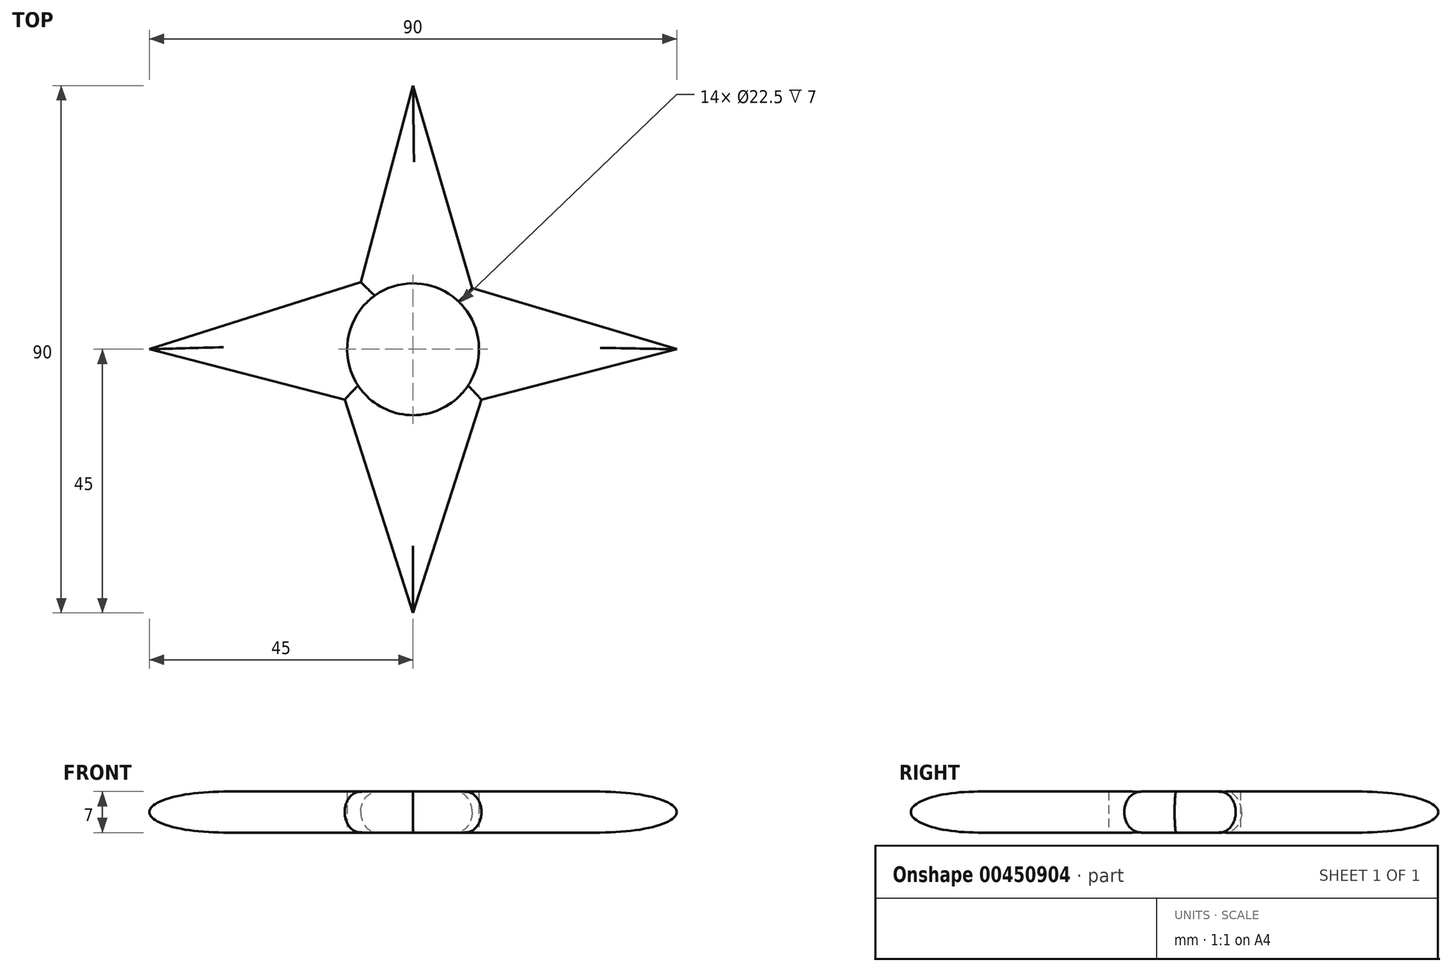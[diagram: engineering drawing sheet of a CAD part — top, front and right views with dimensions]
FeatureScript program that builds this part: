
annotation { "Feature Type Name" : "Feature", "Feature Type Description" : "" }
export const myFeature = defineFeature(function(context is Context, id is Id, definition is map)
    precondition{}
    {
        {
            var Q0;
            Q0=qCreatedBy(makeId("Top.planeOp"),FACE);
            var sketch = newSketch(context, id + "F0", { "sketchPlane" : qUnion([Q0])});
            skCircle(sketch, "E0", {"center": v(0, 0) * mm, "radius": 11.25 * mm});
            skCircle(sketch, "E1", {"center": v(0, 0) * mm, "radius": 14.5 * mm});
            skLineSegment(sketch, "E2", {"start": v(10.08, 10.43) * mm, "end": v(45, 0) * mm});
            skLineSegment(sketch, "E3", {"start": v(45, 0) * mm, "end": v(11.67, -8.6) * mm});
            skLineSegment(sketch, "E4", {"start": v(-11.67, -8.6) * mm, "end": v(-45, 0) * mm});
            skLineSegment(sketch, "E5", {"start": v(-45, 0) * mm, "end": v(-8.92, 11.43) * mm});
            skLineSegment(sketch, "E6", {"start": v(-8.92, 11.43) * mm, "end": v(0, 45) * mm});
            skLineSegment(sketch, "E7", {"start": v(0, 45) * mm, "end": v(10.08, 10.43) * mm});
            skLineSegment(sketch, "E8", {"start": v(-11.67, -8.6) * mm, "end": v(0, -45) * mm});
            skLineSegment(sketch, "E9", {"start": v(0, -45) * mm, "end": v(11.67, -8.6) * mm});
            skSolve(sketch);
        }
        {
            var Q0;
            Q0 = qSketchRegion(id + "F0", true);
            extrude(context, id + "F1", {"entities" : qUnion([Q0]), "depth" : 7 * mm});
        }
        {
            var Q0;
            Q0=makeQuery(id+"F1.opExtrude","CAP_EDGE",EDGE,{"disambiguationData":[OSD([sQuery(id+"F0.wireOp",EDGE,"E7")])],"isStart":false});
            var Q1;
            Q1=makeQuery(id+"F1.opExtrude","CAP_EDGE",EDGE,{"disambiguationData":[OSD([sQuery(id+"F0.wireOp",EDGE,"E6")])],"isStart":false});
            var Q2;
            Q2=makeQuery(id+"F1.opExtrude","CAP_EDGE",EDGE,{"disambiguationData":[OSD([sQuery(id+"F0.wireOp",EDGE,"E5")])],"isStart":false});
            var Q3;
            Q3=makeQuery(id+"F1.opExtrude","CAP_EDGE",EDGE,{"disambiguationData":[OSD([sQuery(id+"F0.wireOp",EDGE,"E4")])],"isStart":false});
            var Q4;
            Q4=makeQuery(id+"F1.opExtrude","CAP_EDGE",EDGE,{"disambiguationData":[OSD([sQuery(id+"F0.wireOp",EDGE,"E8")])],"isStart":false});
            var Q5;
            Q5=makeQuery(id+"F1.opExtrude","CAP_EDGE",EDGE,{"disambiguationData":[OSD([sQuery(id+"F0.wireOp",EDGE,"E9")])],"isStart":false});
            var Q6;
            Q6=makeQuery(id+"F1.opExtrude","CAP_EDGE",EDGE,{"disambiguationData":[OSD([sQuery(id+"F0.wireOp",EDGE,"E3")])],"isStart":false});
            var Q7;
            Q7=makeQuery(id+"F1.opExtrude","CAP_EDGE",EDGE,{"disambiguationData":[OSD([sQuery(id+"F0.wireOp",EDGE,"E2")])],"isStart":false});
            fillet(context, id + "F2", {"entities" : qUnion([Q0, Q1, Q2, Q3, Q4, Q5, Q6, Q7]), "radius" : 3.5 * mm, "tangentPropagation" : true, "allowEdgeOverflow" : false});
        }
        {
            var Q0;
            Q0=makeQuery(id+"F1.opExtrude","CAP_EDGE",EDGE,{"disambiguationData":[OSD([sQuery(id+"F0.wireOp",EDGE,"E7")])],"isStart":true});
            var Q1;
            Q1=makeQuery(id+"F1.opExtrude","CAP_EDGE",EDGE,{"disambiguationData":[OSD([sQuery(id+"F0.wireOp",EDGE,"E2")])],"isStart":true});
            var Q2;
            Q2=makeQuery(id+"F1.opExtrude","CAP_EDGE",EDGE,{"disambiguationData":[OSD([sQuery(id+"F0.wireOp",EDGE,"E3")])],"isStart":true});
            var Q3;
            Q3=makeQuery(id+"F1.opExtrude","CAP_EDGE",EDGE,{"disambiguationData":[OSD([sQuery(id+"F0.wireOp",EDGE,"E9")])],"isStart":true});
            var Q4;
            Q4=makeQuery(id+"F1.opExtrude","CAP_EDGE",EDGE,{"disambiguationData":[OSD([sQuery(id+"F0.wireOp",EDGE,"E8")])],"isStart":true});
            var Q5;
            Q5=makeQuery(id+"F1.opExtrude","CAP_EDGE",EDGE,{"disambiguationData":[OSD([sQuery(id+"F0.wireOp",EDGE,"E4")])],"isStart":true});
            var Q6;
            Q6=makeQuery(id+"F1.opExtrude","CAP_EDGE",EDGE,{"disambiguationData":[OSD([sQuery(id+"F0.wireOp",EDGE,"E5")])],"isStart":true});
            var Q7;
            Q7=makeQuery(id+"F1.opExtrude","CAP_EDGE",EDGE,{"disambiguationData":[OSD([sQuery(id+"F0.wireOp",EDGE,"E6")])],"isStart":true});
            fillet(context, id + "F3", {"entities" : qUnion([Q0, Q1, Q2, Q3, Q4, Q5, Q6, Q7]), "radius" : 3.5 * mm, "tangentPropagation" : true, "allowEdgeOverflow" : false});
        }
    });
